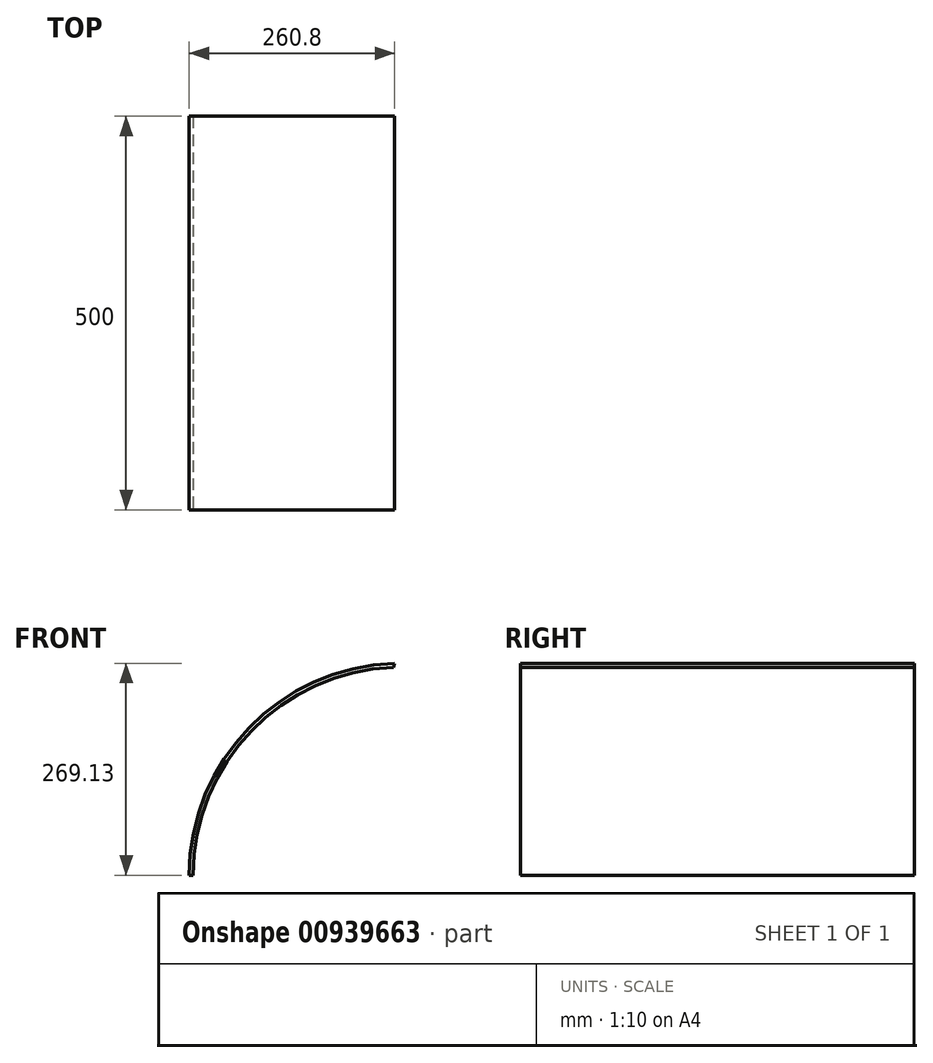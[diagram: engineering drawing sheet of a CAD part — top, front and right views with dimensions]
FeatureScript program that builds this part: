
annotation { "Feature Type Name" : "Feature", "Feature Type Description" : "" }
export const myFeature = defineFeature(function(context is Context, id is Id, definition is map)
    precondition{}
    {
        {
            var Q0;
            Q0=qCreatedBy(makeId("Front.planeOp"),FACE);
            var sketch = newSketch(context, id + "F0", { "sketchPlane" : qUnion([Q0])});
            skArc(sketch, "E0", {"start": v(241.54, 269.13) * mm, "mid": v(56.64, 187.38) * mm, "end": v(-19.26, 0) * mm});
            skLineSegment(sketch, "E1.bottom", {"start": v(-19.26, 0) * mm, "end": v(-14.26, 0) * mm});
            skArc(sketch, "E2", {"start": v(-14.26, 0) * mm, "mid": v(59.62, 183.27) * mm, "end": v(239.94, 264.07) * mm});
            skLineSegment(sketch, "E3", {"start": v(239.94, 264.07) * mm, "end": v(241.54, 269.13) * mm});
            skSolve(sketch);
        }
        {
            var Q0;
            Q0=qSketchRegion(id+"F0",true);
            extrude(context, id + "F1", {"entities" : qUnion([Q0]), "oppositeDirection" : true, "depth" : 6 * mm, "offsetDistance" : 25 * mm});
        }
        {
            var Q0;
            Q0=qSketchRegion(id+"F0",true);
            var Q1;
            Q1=makeQuery(id+"F1.opExtrude","CAP_FACE",FACE,{"disambiguationData":[OSD([sQuery(id+"F0.wireOp",EDGE,"E0"),sQuery(id+"F0.wireOp",EDGE,"E2"),sQuery(id+"F0.wireOp",EDGE,"E3"),sQuery(id+"F0.wireOp",EDGE,"E1.bottom")])],"isStart":true});
            extrude(context, id + "F2", {"entities" : qUnion([Q0, Q1]), "operationType" : NewBodyOperationType.ADD, "oppositeDirection" : true, "depth" : 500 * mm, "offsetDistance" : 25 * mm});
        }
    });
